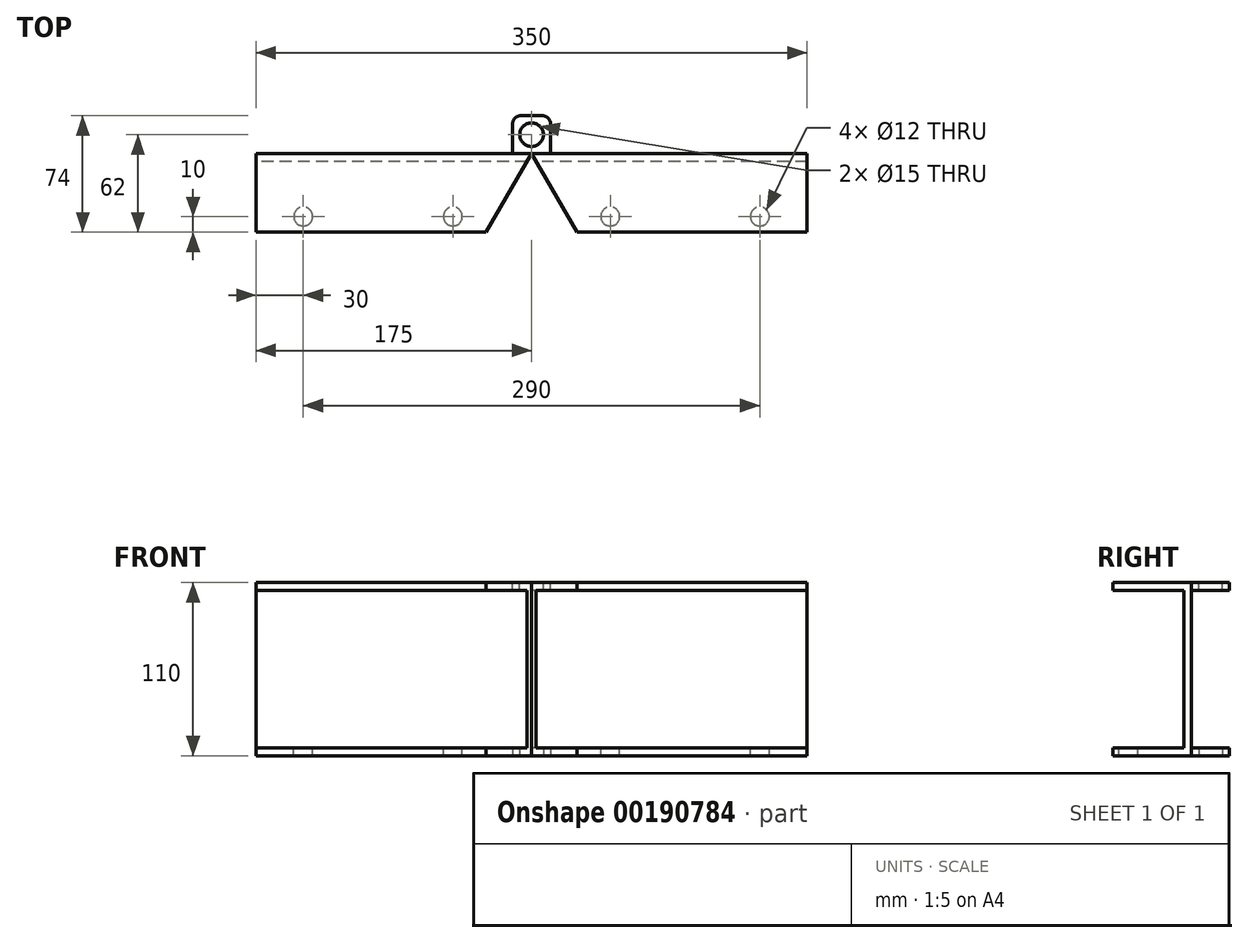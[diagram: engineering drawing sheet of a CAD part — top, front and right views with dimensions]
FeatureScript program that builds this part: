
annotation { "Feature Type Name" : "Feature", "Feature Type Description" : "" }
export const myFeature = defineFeature(function(context is Context, id is Id, definition is map)
    precondition{}
    {
        {
            var Q0;
            Q0=qCreatedBy(makeId("Front.planeOp"),FACE);
            var sketch = newSketch(context, id + "F0", { "sketchPlane" : qUnion([Q0])});
            skLineSegment(sketch, "E0.bottom", {"start": v(175, 55) * mm, "end": v(-175, 55) * mm});
            skLineSegment(sketch, "E0.top", {"start": v(175, -55) * mm, "end": v(-175, -55) * mm});
            skLineSegment(sketch, "E0.left", {"start": v(175, 55) * mm, "end": v(175, -55) * mm});
            skLineSegment(sketch, "E0.right", {"start": v(-175, 55) * mm, "end": v(-175, -55) * mm});
            skPoint(sketch, "E0.middle", {"position": v(0, 0) * mm});
            skSolve(sketch);
        }
        {
            var Q0;
            Q0=makeQuery(id+"F0.imprint","IMPRINT",FACE,{"disambiguationData":[TD([[makeQuery(id+"F0.imprint","IMPRINT",EDGE,{"derivedFrom":sQuery(id+"F0.wireOp",EDGE,"E0.bottom")}),1.0]])]});
            extrude(context, id + "F1", {"entities" : qUnion([Q0]), "endBound" : BoundingType.SYMMETRIC, "depth" : 50 * mm});
        }
        {
            var Q0;
            Q0=makeQuery(id+"F1.opExtrude","SWEPT_FACE",FACE,{"disambiguationData":[OSD([sQuery(id+"F0.wireOp",EDGE,"E0.bottom")])]});
            var sketch = newSketch(context, id + "F2", { "sketchPlane" : qUnion([Q0])});
            skLineSegment(sketch, "E1", {"start": v(0, 25) * mm, "end": v(-28.87, -25) * mm});
            skLineSegment(sketch, "E2.MirrorCS", {"start": v(0, 25) * mm, "end": v(28.87, -25) * mm});
            skSolve(sketch);
        }
        {
            var Q0;
            {var subQ0=sQuery(id+"F2.wireOp",EDGE,"E1");Q0=makeQuery(id+"F2.imprint","IMPRINT",FACE,{"disambiguationData":[TD([[makeQuery(id+"F2.imprint","IMPRINT",EDGE,{"derivedFrom":subQ0}),1.0]])]});}
            extrude(context, id + "F3", {"entities" : qUnion([Q0]), "operationType" : NewBodyOperationType.REMOVE, "endBound" : BoundingType.THROUGH_ALL, "oppositeDirection" : true, "depth" : 25 * mm});
        }
        {
            var Q0;
            {var subQ0=sQuery(id+"F0.wireOp",EDGE,"E0.bottom");var subQ1=sQuery(id+"F0.wireOp",EDGE,"E0.top");var subQ2=sQuery(id+"F0.wireOp",EDGE,"E0.right");Q0=makeQuery(id+"F3.boolean.opBoolean","SPLIT",FACE,{"disambiguationData":[TD([makeQuery(id+"F1.opExtrude","SWEPT_FACE",FACE,{"disambiguationData":[OSD([subQ2])]})])],"derivedFrom":makeQuery(id+"F1.opExtrude","CAP_FACE",FACE,{"disambiguationData":[OSD([subQ0,subQ1,sQuery(id+"F0.wireOp",EDGE,"E0.left"),subQ2])],"isStart":false})});}
            var sketch = newSketch(context, id + "F4", { "sketchPlane" : qUnion([Q0])});
            skLineSegment(sketch, "E3.bottom", {"start": v(191.42, 50) * mm, "end": v(-191.42, 50) * mm});
            skLineSegment(sketch, "E3.top", {"start": v(191.42, -50) * mm, "end": v(-191.42, -50) * mm});
            skLineSegment(sketch, "E3.left", {"start": v(191.42, 50) * mm, "end": v(191.42, -50) * mm});
            skLineSegment(sketch, "E3.right", {"start": v(-191.42, 50) * mm, "end": v(-191.42, -50) * mm});
            skPoint(sketch, "E3.middle", {"position": v(0, 0) * mm});
            skSolve(sketch);
        }
        {
            var Q0;
            {var subQ0=sQuery(id+"F4.wireOp",EDGE,"E3.right");Q0=makeQuery(id+"F4.imprint","IMPRINT",FACE,{"disambiguationData":[TD([[makeQuery(id+"F4.imprint","IMPRINT",EDGE,{"derivedFrom":subQ0}),1.0]])]});}
            var Q1;
            {var subQ0=sQuery(id+"F4.wireOp",EDGE,"E3.left");Q1=makeQuery(id+"F4.imprint","IMPRINT",FACE,{"disambiguationData":[TD([[makeQuery(id+"F4.imprint","IMPRINT",EDGE,{"derivedFrom":subQ0}),-1.0]])]});}
            var Q2;
            {var subQ0=sQuery(id+"F4.wireOp",EDGE,"E3.bottom");var subQ3=makeQuery(id+"F1.opExtrude","CAP_EDGE",EDGE,{"disambiguationData":[OSD([sQuery(id+"F0.wireOp",EDGE,"E0.right")])],"isStart":false});var subQ4=makeQuery(id+"F4.imprint","INTERSECT",VERTEX,{"derivedFrom":[subQ3,subQ0]});Q2=makeQuery(id+"F4.imprint","IMPRINT",FACE,{"disambiguationData":[TD([[makeQuery(id+"F4.imprint","IMPRINT",EDGE,{"disambiguationData":[TD([[subQ4,-1.0]])],"derivedFrom":subQ3}),1.0]])]});}
            extrude(context, id + "F5", {"entities" : qUnion([Q0, Q1, Q2]), "operationType" : NewBodyOperationType.REMOVE, "oppositeDirection" : true, "depth" : 45 * mm});
        }
        {
            var Q0;
            {var subQ0=sQuery(id+"F4.wireOp",EDGE,"E3.left");Q0=makeQuery(id+"F4.imprint","IMPRINT",FACE,{"disambiguationData":[TD([[makeQuery(id+"F4.imprint","IMPRINT",EDGE,{"derivedFrom":subQ0}),-1.0]])]});}
            extrude(context, id + "F6", {"entities" : qUnion([Q0]), "operationType" : NewBodyOperationType.REMOVE, "oppositeDirection" : true, "depth" : 45 * mm});
        }
        {
            var Q0;
            {var subQ1=sQuery(id+"F0.wireOp",EDGE,"E0.left");var subQ3=sQuery(id+"F0.wireOp",EDGE,"E0.bottom");Q0=makeQuery(id+"F3.boolean.opBoolean","SPLIT",FACE,{"disambiguationData":[TD([makeQuery(id+"F1.opExtrude","SWEPT_FACE",FACE,{"disambiguationData":[OSD([subQ1])]})])],"derivedFrom":makeQuery(id+"F1.opExtrude","SWEPT_FACE",FACE,{"disambiguationData":[OSD([subQ3])]})});}
            var sketch = newSketch(context, id + "F7", { "sketchPlane" : qUnion([Q0])});
            skLineSegment(sketch, "E4", {"start": v(12, 25) * mm, "end": v(12, 44) * mm});
            skLineSegment(sketch, "E5", {"start": v(7, 49) * mm, "end": v(-7, 49) * mm});
            skLineSegment(sketch, "E6", {"start": v(-12, 44) * mm, "end": v(-12, 25) * mm});
            skCircle(sketch, "E7", {"center": v(0, 37) * mm, "radius": 7.5 * mm});
            skPoint(sketch, "E8.visualSharp", {"position": v(-12, 49) * mm});
            skArc(sketch, "E8.filletArc", {"start": v(-7, 49) * mm, "mid": v(-10.54, 47.54) * mm, "end": v(-12, 44) * mm});
            skPoint(sketch, "E9.visualSharp", {"position": v(12, 49) * mm});
            skArc(sketch, "E9.filletArc", {"start": v(12, 44) * mm, "mid": v(10.54, 47.54) * mm, "end": v(7, 49) * mm});
            skLineSegment(sketch, "E10", {"start": v(-12, 25) * mm, "end": v(12, 25) * mm});
            skSolve(sketch);
        }
        {
            var Q0;
            {var subQ1=sQuery(id+"F7.wireOp",EDGE,"E4");Q0=makeQuery(id+"F7.imprint","IMPRINT",FACE,{"disambiguationData":[TD([[makeQuery(id+"F7.imprint","IMPRINT",EDGE,{"derivedFrom":subQ1}),1.0]])]});}
            extrude(context, id + "F8", {"entities" : qUnion([Q0]), "oppositeDirection" : true, "depth" : 5 * mm});
        }
        {
            var Q0;
            Q0=qCreatedBy(makeId("Top.planeOp"),FACE);
            var sketch = newSketch(context, id + "F9", { "sketchPlane" : qUnion([Q0])});
            skPoint(sketch, "E11", {"position": v(-145, -15) * mm});
            skPoint(sketch, "E12", {"position": v(-50, -15) * mm});
            skPoint(sketch, "E13.MirrorP", {"position": v(50, -15) * mm});
            skPoint(sketch, "E14.MirrorP", {"position": v(145, -15) * mm});
            skSolve(sketch);
        }
        {
            var Q0;
            Q0=sQuery(id+"F9.wireOp",VERTEX,"E11");
            var Q1;
            Q1=sQuery(id+"F9.wireOp",VERTEX,"E12");
            var Q2;
            Q2=sQuery(id+"F9.wireOp",VERTEX,"E13.MirrorP");
            var Q3;
            Q3=sQuery(id+"F9.wireOp",VERTEX,"E14.MirrorP");
            var Q4;
            Q4=makeQuery(id+"F3.boolean.opBoolean","SPLIT",BODY,{"disambiguationData":[OD(1.0)],"derivedFrom":makeQuery(id+"F1.opExtrude","SWEPT_BODY",BODY,{"disambiguationData":[OSD([sQuery(id+"F0.wireOp",EDGE,"E0.bottom"),sQuery(id+"F0.wireOp",EDGE,"E0.top"),sQuery(id+"F0.wireOp",EDGE,"E0.left"),sQuery(id+"F0.wireOp",EDGE,"E0.right")])]})});
            var Q5;
            Q5=makeQuery(id+"F3.boolean.opBoolean","SPLIT",BODY,{"disambiguationData":[OD(0.0)],"derivedFrom":makeQuery(id+"F1.opExtrude","SWEPT_BODY",BODY,{"disambiguationData":[OSD([sQuery(id+"F0.wireOp",EDGE,"E0.bottom"),sQuery(id+"F0.wireOp",EDGE,"E0.top"),sQuery(id+"F0.wireOp",EDGE,"E0.left"),sQuery(id+"F0.wireOp",EDGE,"E0.right")])]})});
            hole(context, id + "F10", {"style" : HoleStyle.SIMPLE, "endStyle" : HoleEndStyle.THROUGH, "standardTappedOrClearance" : lookupTablePath({ "standard" : "ISO", "size" : "12", "type" : "Drilled" }), "standardBlindInLast" : lookupTablePath({ "standard" : "ISO", "size" : "12", "type" : "Drilled" }), "holeDiameter" : 12 * mm, "locations" : qUnion([Q0, Q1, Q2, Q3]), "scope" : qUnion([Q4, Q5]), "isTappedThrough" : true});
        }
        {
            var Q0;
            Q0=makeQuery(id+"F8.opExtrude","SWEPT_BODY",BODY,{"disambiguationData":[OSD([sQuery(id+"F7.wireOp",EDGE,"E4"),sQuery(id+"F7.wireOp",EDGE,"E5"),sQuery(id+"F7.wireOp",EDGE,"E6"),sQuery(id+"F7.wireOp",EDGE,"E7"),sQuery(id+"F7.wireOp",EDGE,"E8.filletArc"),sQuery(id+"F7.wireOp",EDGE,"E9.filletArc"),sQuery(id+"F7.wireOp",EDGE,"E10")])]});
            var Q1;
            Q1=qCreatedBy(makeId("Top.planeOp"),FACE);
            mirror(context, id + "F11", {"entities" : qUnion([Q0]), "mirrorPlane" : qUnion([Q1])});
        }
    });
